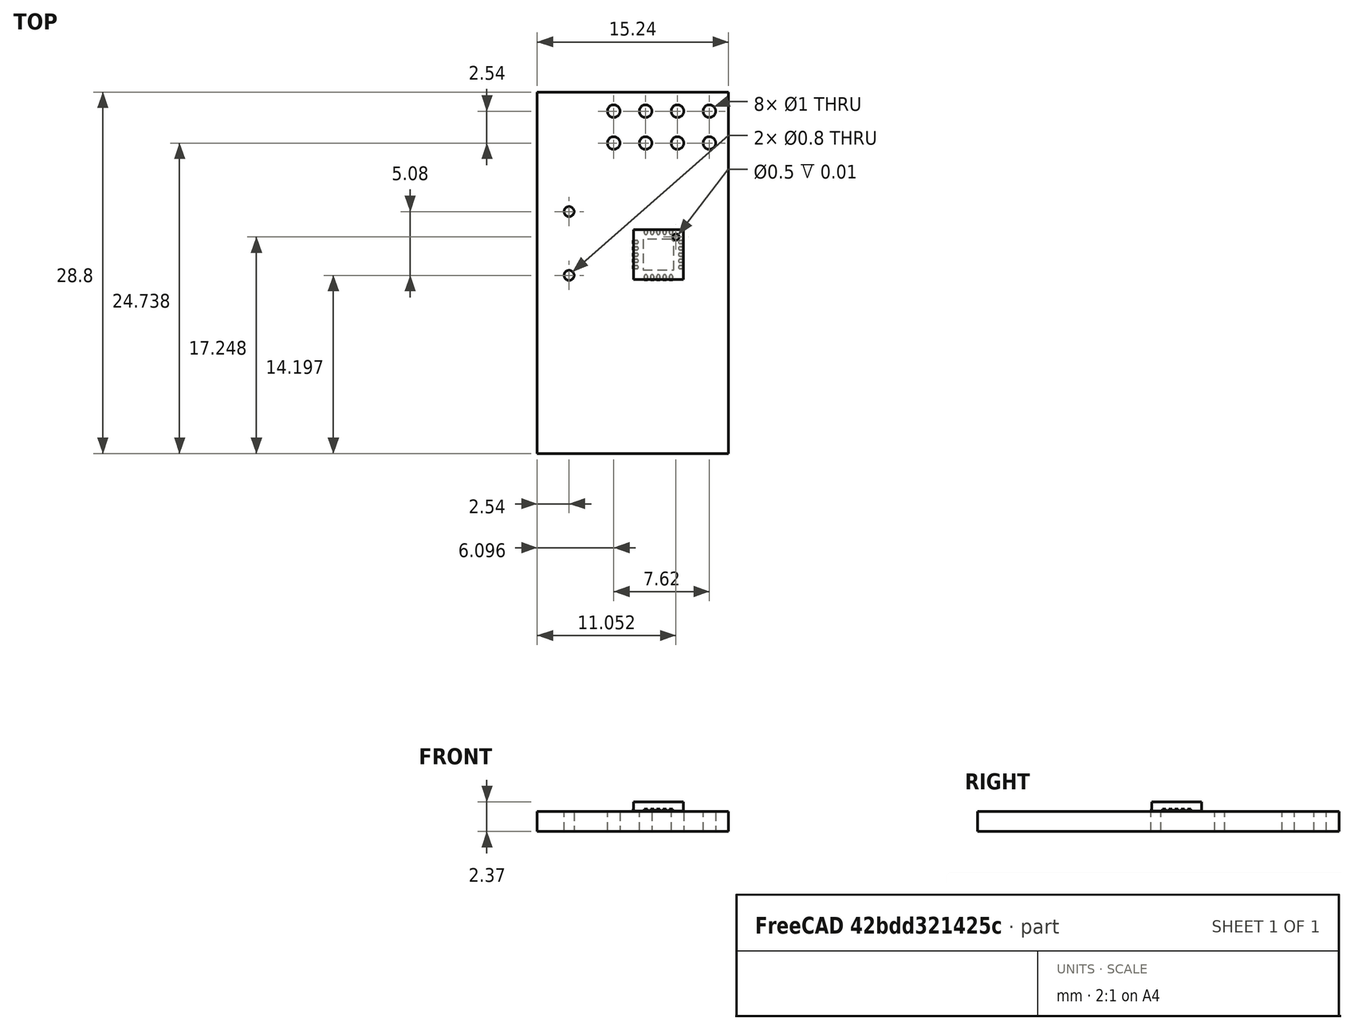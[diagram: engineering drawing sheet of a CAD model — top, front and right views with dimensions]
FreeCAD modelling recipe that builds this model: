
FCSTD DOCUMENT  (FreeCAD 0.17R13509 (Git))
Label: nrf24l01
License: All rights reserved
LicenseURL: http://en.wikipedia.org/wiki/All_rights_reserved
objects: App::Part×4, Part::Feature×2, Sketcher::SketchObject×1
note: 3 computed .brp shape members not serialized (recipe doc carries the construction recipe); baked Part::Feature solids carry a one-line shape summary decoded from their .brp

FEATURE [Part::Feature] Pcb
  Placement = pos=(-127.254,88.9508,0) rot=(0,0,1;0rad)
  shape: bbox 15.25 x 28.81 x 1.61 mm, 16 faces (baked)
FEATURE [Sketcher::SketchObject] PCB_Sketch
  sketch-geometry (4):
    g0: LineSegment StartX=-7.62 StartY=-14.4018 StartZ=0 EndX=-7.62 EndY=14.4018 EndZ=0
    g1: LineSegment StartX=7.62 StartY=-14.4018 StartZ=0 EndX=-7.62 EndY=-14.4018 EndZ=0
    g2: LineSegment StartX=7.62 StartY=14.4018 StartZ=0 EndX=7.62 EndY=-14.4018 EndZ=0
    g3: LineSegment StartX=-7.62 StartY=14.4018 StartZ=0 EndX=7.62 EndY=14.4018 EndZ=0
  constraints (8):
    c: Vertical(g0)
    c: Coincident(g0,g1)
    c: Coincident(g0,g3)
    c: Horizontal(g1)
    c: Coincident(g1,g2)
    c: Vertical(g2)
    c: Coincident(g2,g3)
    c: Horizontal(g3)
FEATURE [App::Part] Board_Geoms
  Group = -> [Pcb,PCB_Sketch]
  Origin = -> Origin
FEATURE [Part::Feature] Shape  label="QFN-20-1EP_4x4mm_Pitch0.5mm_"
  Placement = pos=(2.032,1.4478,0) rot=(0,0,-1;1.5708rad)
  shape: bbox 4 x 4 x 0.77 mm, 134 faces (baked)
FEATURE [App::Part] Top
  Group = -> [Shape]
  License = CC BY 3.0
  LicenseURL = http://creativecommons.org/licenses/by/3.0/
  Origin = -> Origin003
FEATURE [App::Part] Step_Models
  Group = -> [Top]
  Origin = -> Origin002
FEATURE [App::Part] Board  label="nrf24l01"
  Group = -> [Board_Geoms,Step_Models]
  Origin = -> Origin001
